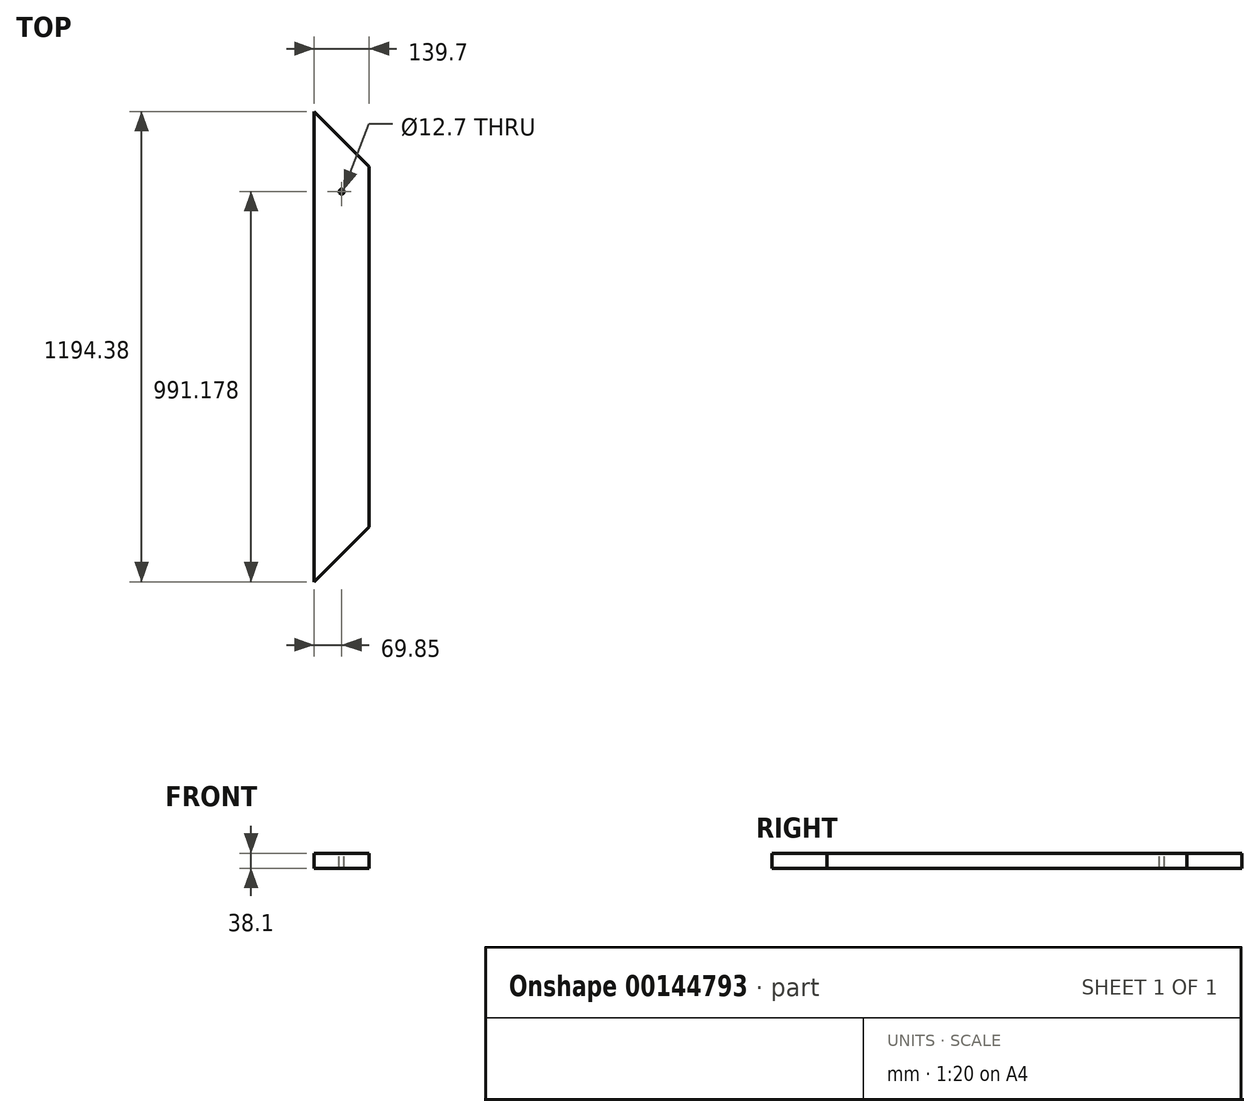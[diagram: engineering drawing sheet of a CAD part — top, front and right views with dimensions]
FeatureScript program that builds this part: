
annotation { "Feature Type Name" : "Feature", "Feature Type Description" : "" }
export const myFeature = defineFeature(function(context is Context, id is Id, definition is map)
    precondition{}
    {
        {
            var Q0;
            Q0=qCreatedBy(makeId("Front.planeOp"),FACE);
            var sketch = newSketch(context, id + "F0", { "sketchPlane" : qUnion([Q0])});
            skLineSegment(sketch, "E0.bottom", {"start": v(0, 0) * mm, "end": v(139.7, 0) * mm});
            skLineSegment(sketch, "E0.top", {"start": v(0, 38.1) * mm, "end": v(139.7, 38.1) * mm});
            skLineSegment(sketch, "E0.left", {"start": v(0, 0) * mm, "end": v(0, 38.1) * mm});
            skLineSegment(sketch, "E0.right", {"start": v(139.7, 0) * mm, "end": v(139.7, 38.1) * mm});
            skSolve(sketch);
        }
        {
            var Q0;
            Q0=makeQuery(id+"F0.imprint","IMPRINT",FACE,{"disambiguationData":[TD([[makeQuery(id+"F0.imprint","IMPRINT",EDGE,{"derivedFrom":sQuery(id+"F0.wireOp",EDGE,"E0.bottom")}),1.0]])]});
            extrude(context, id + "F1", {"entities" : qUnion([Q0]), "depth" : 1828.8 * mm});
        }
        {
            var Q0;
            Q0=makeQuery(id+"F1.opExtrude","CAP_FACE",FACE,{"disambiguationData":[OSD([sQuery(id+"F0.wireOp",EDGE,"E0.bottom"),sQuery(id+"F0.wireOp",EDGE,"E0.top"),sQuery(id+"F0.wireOp",EDGE,"E0.left"),sQuery(id+"F0.wireOp",EDGE,"E0.right")])],"isStart":false});
            var Q1;
            Q1=makeQuery(id+"F1.opExtrude","CAP_EDGE",EDGE,{"disambiguationData":[OSD([sQuery(id+"F0.wireOp",EDGE,"E0.right")])],"isStart":false});
            cPlane(context, id + "F2", {"entities" : qUnion([Q0, Q1]), "cplaneType" : CPlaneType.LINE_ANGLE, "offset" : 25.4 * mm, "angle" : 45 * degree, "width" : 152.4 * mm, "height" : 152.4 * mm});
        }
        {
            var Q0;
            Q0=qCreatedBy(id+"F2.planeOp",FACE);
            var sketch = newSketch(context, id + "F3", { "sketchPlane" : qUnion([Q0])});
            skLineSegment(sketch, "E1.bottom", {"start": v(1388.33, 137.34) * mm, "end": v(1057.01, 137.34) * mm});
            skLineSegment(sketch, "E1.top", {"start": v(1388.33, -123.24) * mm, "end": v(1057.01, -123.24) * mm});
            skLineSegment(sketch, "E1.left", {"start": v(1388.33, 137.34) * mm, "end": v(1388.33, -123.24) * mm});
            skLineSegment(sketch, "E1.right", {"start": v(1057.01, 137.34) * mm, "end": v(1057.01, -123.24) * mm});
            skSolve(sketch);
        }
        {
            var Q0;
            Q0 = qSketchRegion(id + "F3", true);
            extrude(context, id + "F4", {"entities" : qUnion([Q0]), "operationType" : NewBodyOperationType.REMOVE, "depth" : 101.6 * mm});
        }
        {
            var Q0;
            Q0=makeQuery(id+"F4.boolean.opBoolean","INTERSECT",EDGE,{"derivedFrom":[makeQuery(id+"F1.opExtrude","SWEPT_FACE",FACE,{"disambiguationData":[OSD([sQuery(id+"F0.wireOp",EDGE,"E0.left")])]}),makeQuery(id+"F4.opExtrude","CAP_FACE",FACE,{"disambiguationData":[OSD([sQuery(id+"F3.wireOp",EDGE,"E1.bottom"),sQuery(id+"F3.wireOp",EDGE,"E1.top"),sQuery(id+"F3.wireOp",EDGE,"E1.left"),sQuery(id+"F3.wireOp",EDGE,"E1.right")])],"isStart":false})]});
            cPlane(context, id + "F5", {"entities" : qUnion([Q0]), "cplaneType" : CPlaneType.LINE_ANGLE, "offset" : 25.4 * mm, "angle" : 315 * degree, "width" : 152.4 * mm, "height" : 152.4 * mm});
        }
        {
            var Q0;
            Q0=qCreatedBy(id+"F5.planeOp",FACE);
            cPlane(context, id + "F6", {"entities" : qUnion([Q0]), "cplaneType" : CPlaneType.OFFSET, "offset" : 844.55 * mm, "oppositeDirection" : true, "width" : 152.4 * mm, "height" : 152.4 * mm});
        }
        {
            var Q0;
            Q0=qCreatedBy(id+"F6.planeOp",FACE);
            var sketch = newSketch(context, id + "F7", { "sketchPlane" : qUnion([Q0])});
            skLineSegment(sketch, "E2.bottom", {"start": v(-162.29, 396.16) * mm, "end": v(1391.17, 396.16) * mm});
            skLineSegment(sketch, "E2.top", {"start": v(-162.29, -759.2) * mm, "end": v(1391.17, -759.2) * mm});
            skLineSegment(sketch, "E2.left", {"start": v(-162.29, 396.16) * mm, "end": v(-162.29, -759.2) * mm});
            skLineSegment(sketch, "E2.right", {"start": v(1391.17, 396.16) * mm, "end": v(1391.17, -759.2) * mm});
            skSolve(sketch);
        }
        {
            var Q0;
            Q0=makeQuery(id+"F7.imprint","IMPRINT",FACE,{"disambiguationData":[TD([[makeQuery(id+"F7.imprint","IMPRINT",EDGE,{"derivedFrom":sQuery(id+"F7.wireOp",EDGE,"E2.bottom")}),-1.0]])]});
            extrude(context, id + "F8", {"entities" : qUnion([Q0]), "operationType" : NewBodyOperationType.REMOVE, "oppositeDirection" : true, "depth" : 762 * mm});
        }
        {
            var Q0;
            Q0=makeQuery(id+"F1.opExtrude","SWEPT_FACE",FACE,{"disambiguationData":[OSD([sQuery(id+"F0.wireOp",EDGE,"E0.top")])]});
            var sketch = newSketch(context, id + "F9", { "sketchPlane" : qUnion([Q0])});
            skCircle(sketch, "E3", {"center": v(69.85, -833.64) * mm, "radius": 6.35 * mm});
            skSolve(sketch);
        }
        {
            var Q0;
            Q0=makeQuery(id+"F9.imprint","IMPRINT",FACE,{"disambiguationData":[TD([[makeQuery(id+"F9.imprint","IMPRINT",EDGE,{"derivedFrom":sQuery(id+"F9.wireOp",EDGE,"wap9MuZf-Jf07-LpLO-fPMC-GmTDpLo85pdL.bottom")}),-1.0]])]});
            var Q1;
            Q1=makeQuery(id+"F9.imprint","IMPRINT",FACE,{"disambiguationData":[TD([[makeQuery(id+"F9.imprint","IMPRINT",EDGE,{"derivedFrom":sQuery(id+"F9.wireOp",EDGE,"E3")}),1.0]])]});
            extrude(context, id + "F10", {"entities" : qUnion([Q0, Q1]), "operationType" : NewBodyOperationType.REMOVE, "endBound" : BoundingType.THROUGH_ALL, "oppositeDirection" : true, "depth" : 25.4 * mm});
        }
    });
